# Revit family: NBS_wediSystemsUKLtd_Stng_SanoasaComoda_BenchCornerElement
name_source: partatom
category: Furniture
revit_build: Autodesk Revit 2018 (Build: 20190510_1515(x64)
units: mm (PartAtom-declared; Revit-internal decimal feet)

## family parameters
Always vertical = Yes
Cut with Voids When Loaded = No
Room Calculation Point = No
Shared = No
Work Plane-Based = No

## types (1)
- BenchCornerElement_Straight_90
    AssetType = Fixed
    BIMObjectName = NBS_wediSystemsUKLtd_Seating_SanoasaComoda_BenchCornerElement_Straight_90
    BenchMaterial = NBS_Concept
    Category = Pr_40_20_06_83:Shower seats
    Color = Grey
    Description = Sanoasa Comoda, bench corner element 90°, straight
    DurationUnit = year
    ExpectedLife = 30
    Features = Sanoasa Comoda benches are available in so many different designs, meaning that they can be built into almost any seating combination
    Finish = resistant and glass fibre reinforced cement coating
    Form = Practical wellness benches with modular construction
    IfcExportAs = IfcFurnitureType
    IfcExportType = SOFA
    IsBuiltIn = Yes
    MainColor = Grey
    ManufacturerName = wedi Systems (UK) Ltd
    ManufacturerURL = https://www.wedi.de
    Material = A waterproof extruded polystyrene rigid foam core with a special, resistant and glass fibre reinforced cement coating
    MaterialsFrame = A waterproof extruded polystyrene rigid foam core with a special, resistant and glass fibre reinforced cement coating
    MaterialsSeat = A waterproof extruded polystyrene rigid foam core with a special, resistant and glass fibre reinforced cement coating
    ModelNumber = 076447004
    ModelReference = wedi Sanoasa Comoda
    NBSCertification = www.nationalbimlibrary.com/cert/1ienj0yu
    NBSDescription = Seating
    NBSReference = 45-35-72/352
    Name = Seating_wediSanoasaComodaBenchCornerElement_wediSystemsLtd
    NominalDepth = 650 mm  [stored 2.13255 ft]
    NominalHeight = 620 mm  [stored 2.03412 ft]
    NominalLength = 650 mm  [stored 2.13255 ft]
    NominalWidth = 650 mm  [stored 2.13255 ft]
    ProductInformation = https://www.wedi.de
    Size = 650 × 650 × 620 mm
    Status = UNSET
    Style = Bench corner element 90°
    Uniclass2015Code = Pr_40_20_06_83
    Uniclass2015Title = Shower seats
    Uniclass2015Version = Products v1.14
    Version = 2
    WarrantyDescription = available on request
    WarrantyDurationUnit = year

note: [stored X ft] marks values corroborated as IEEE doubles in the binary element streams (Revit-internal decimal feet)

## geometry (parser evidence)
native form markers: Sweep x3
no freeform markers — native parametric forms only
